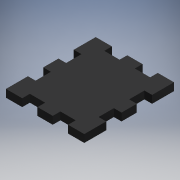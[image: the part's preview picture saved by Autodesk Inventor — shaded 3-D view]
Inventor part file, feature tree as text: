
AUTODESK INVENTOR PART (.ipt)
format: ipt  version: 2019 (Build 230136000, 136)  size: 158,208 bytes
history: native  units: mm
features: extrude x2, sketch x2
ambient origin geometry x8: Origin, YZ Plane, XZ Plane, XY Plane, X Axis, Y Axis, Z Axis, Center Point
bodies: Solid1 (feature_tree)
feature tree (4):
  extrude  "Extrusion1"  Depth=47.0mm
  extrude  "Extrusion2"  Depth=4.0mm
  sketch  "Sketch1"  dims[d0=41.0mm d1=47.0mm]
  sketch  "Sketch2"  dims[d6=4.0mm d7=0.0mm d8=4.0mm d9=8.0mm d10=4.0mm d11=8.0mm d12=4.0mm d13=4.0mm d14=0.0mm]
